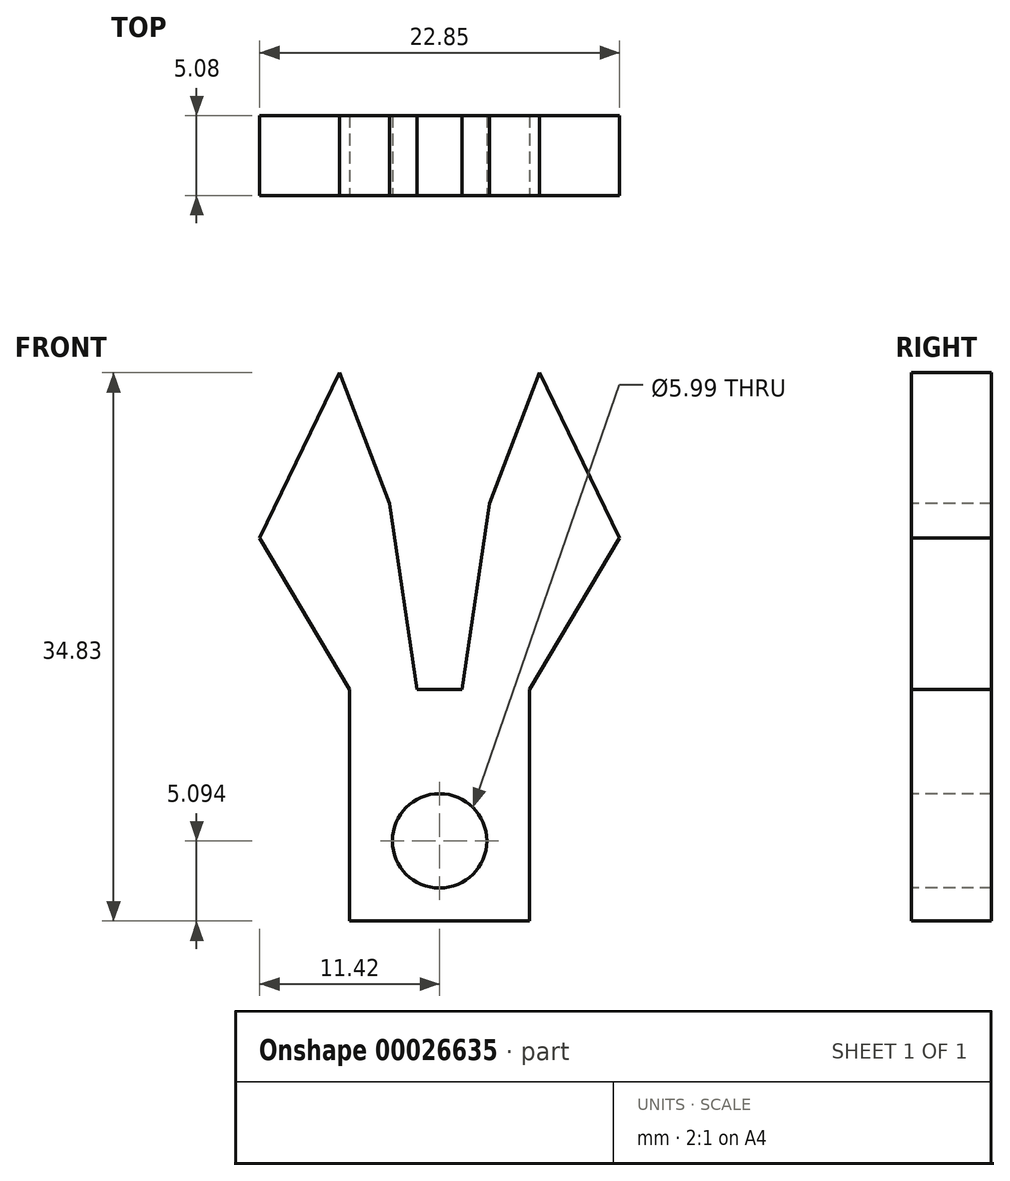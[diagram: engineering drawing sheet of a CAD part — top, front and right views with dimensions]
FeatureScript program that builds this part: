
annotation { "Feature Type Name" : "Feature", "Feature Type Description" : "" }
export const myFeature = defineFeature(function(context is Context, id is Id, definition is map)
    precondition{}
    {
        {
            var Q0;
            Q0=qCreatedBy(makeId("Front.planeOp"),FACE);
            var sketch = newSketch(context, id + "F0", { "sketchPlane" : qUnion([Q0])});
            skLineSegment(sketch, "E0", {"start": v(0, 0) * mm, "end": v(-6.35, 16.6) * mm});
            skLineSegment(sketch, "E1", {"start": v(-6.35, 16.6) * mm, "end": v(6.35, 16.6) * mm});
            skLineSegment(sketch, "E2", {"start": v(6.35, 16.6) * mm, "end": v(0, 0) * mm});
            skLineSegment(sketch, "E3", {"start": v(-6.35, 16.6) * mm, "end": v(-11.42, 6.1) * mm});
            skLineSegment(sketch, "E4", {"start": v(-11.42, 6.1) * mm, "end": v(0, -13.13) * mm});
            skLineSegment(sketch, "E5", {"start": v(0, -13.13) * mm, "end": v(-3.17, 8.3) * mm});
            skLineSegment(sketch, "E6", {"start": v(6.35, 16.6) * mm, "end": v(11.43, 6.11) * mm});
            skLineSegment(sketch, "E7", {"start": v(11.43, 6.11) * mm, "end": v(0, -13.13) * mm});
            skLineSegment(sketch, "E8", {"start": v(0, -13.13) * mm, "end": v(3.18, 8.3) * mm});
            skLineSegment(sketch, "E9", {"start": v(-5.7, -3.51) * mm, "end": v(5.71, -3.51) * mm});
            skLineSegment(sketch, "E10", {"start": v(5.71, -3.51) * mm, "end": v(5.71, -18.22) * mm});
            skLineSegment(sketch, "E11", {"start": v(5.71, -18.22) * mm, "end": v(-5.7, -18.22) * mm});
            skLineSegment(sketch, "E12", {"start": v(-5.7, -3.51) * mm, "end": v(-5.7, -18.22) * mm});
            skCircle(sketch, "E13", {"center": v(0, -13.13) * mm, "radius": 3 * mm});
            skSolve(sketch);
        }
        {
            var Q0;
            {var subQ1=sQuery(id+"F0.wireOp",EDGE,"E6");Q0=makeQuery(id+"F0.imprint","IMPRINT",FACE,{"disambiguationData":[TD([[makeQuery(id+"F0.imprint","IMPRINT",EDGE,{"derivedFrom":subQ1}),-1.0]])]});}
            var Q1;
            {var subQ1=sQuery(id+"F0.wireOp",EDGE,"E3");Q1=makeQuery(id+"F0.imprint","IMPRINT",FACE,{"disambiguationData":[TD([[makeQuery(id+"F0.imprint","IMPRINT",EDGE,{"derivedFrom":subQ1}),1.0]])]});}
            var Q2;
            Q2=makeQuery(id+"F0.imprint","IMPRINT",FACE,{"disambiguationData":[TD([[makeQuery(id+"F0.imprint","IMPRINT",EDGE,{"derivedFrom":sQuery(id+"F0.wireOp",EDGE,"2a0f9860-824c-4955-87cb-d1dbb791d7fb.top")}),1.0]])]});
            var Q3;
            {var subQ0=sQuery(id+"F0.wireOp",EDGE,"2a0f9860-824c-4955-87cb-d1dbb791d7fb.bottom");var subQ1=sQuery(id+"F0.wireOp",EDGE,"E5");var subQ2=makeQuery(id+"F0.imprint","INTERSECT",VERTEX,{"derivedFrom":[subQ1,subQ0]});Q3=makeQuery(id+"F0.imprint","IMPRINT",FACE,{"disambiguationData":[TD([[makeQuery(id+"F0.imprint","IMPRINT",EDGE,{"disambiguationData":[TD([[subQ2,1.0]])],"derivedFrom":subQ0}),-1.0]])]});}
            var Q4;
            {var subQ0=sQuery(id+"F0.wireOp",EDGE,"2a0f9860-824c-4955-87cb-d1dbb791d7fb.bottom");var subQ3=sQuery(id+"F0.wireOp",EDGE,"E7");var subQ4=makeQuery(id+"F0.imprint","INTERSECT",VERTEX,{"derivedFrom":[subQ3,subQ0]});Q4=makeQuery(id+"F0.imprint","IMPRINT",FACE,{"disambiguationData":[TD([[makeQuery(id+"F0.imprint","IMPRINT",EDGE,{"disambiguationData":[TD([[subQ4,1.0]])],"derivedFrom":subQ0}),-1.0]])]});}
            var Q5;
            {var subQ1=sQuery(id+"F0.wireOp",EDGE,"E10");Q5=makeQuery(id+"F0.imprint","IMPRINT",FACE,{"disambiguationData":[TD([[makeQuery(id+"F0.imprint","IMPRINT",EDGE,{"derivedFrom":subQ1}),-1.0]])]});}
            var Q6;
            {var subQ0=sQuery(id+"F0.wireOp",EDGE,"E9");var subQ1=sQuery(id+"F0.wireOp",EDGE,"E5");var subQ2=makeQuery(id+"F0.imprint","INTERSECT",VERTEX,{"derivedFrom":[subQ1,subQ0]});Q6=makeQuery(id+"F0.imprint","IMPRINT",FACE,{"disambiguationData":[TD([[makeQuery(id+"F0.imprint","IMPRINT",EDGE,{"disambiguationData":[TD([[subQ2,1.0]])],"derivedFrom":subQ0}),-1.0]])]});}
            var Q7;
            {var subQ0=sQuery(id+"F0.wireOp",EDGE,"E9");var subQ1=sQuery(id+"F0.wireOp",EDGE,"E8");var subQ2=makeQuery(id+"F0.imprint","INTERSECT",VERTEX,{"derivedFrom":[subQ1,subQ0]});Q7=makeQuery(id+"F0.imprint","IMPRINT",FACE,{"disambiguationData":[TD([[makeQuery(id+"F0.imprint","IMPRINT",EDGE,{"disambiguationData":[TD([[subQ2,-1.0]])],"derivedFrom":subQ0}),-1.0]])]});}
            var Q8;
            {var subQ0=sQuery(id+"F0.wireOp",EDGE,"E9");var subQ3=sQuery(id+"F0.wireOp",EDGE,"E5");var subQ4=makeQuery(id+"F0.imprint","INTERSECT",VERTEX,{"derivedFrom":[subQ3,subQ0]});Q8=makeQuery(id+"F0.imprint","IMPRINT",FACE,{"disambiguationData":[TD([[makeQuery(id+"F0.imprint","IMPRINT",EDGE,{"disambiguationData":[TD([[subQ4,-1.0]])],"derivedFrom":subQ0}),-1.0]])]});}
            extrude(context, id + "F1", {"entities" : qUnion([Q0, Q1, Q2, Q3, Q4, Q5, Q6, Q7, Q8]), "oppositeDirection" : true, "depth" : 5.08 * mm});
        }
    });
